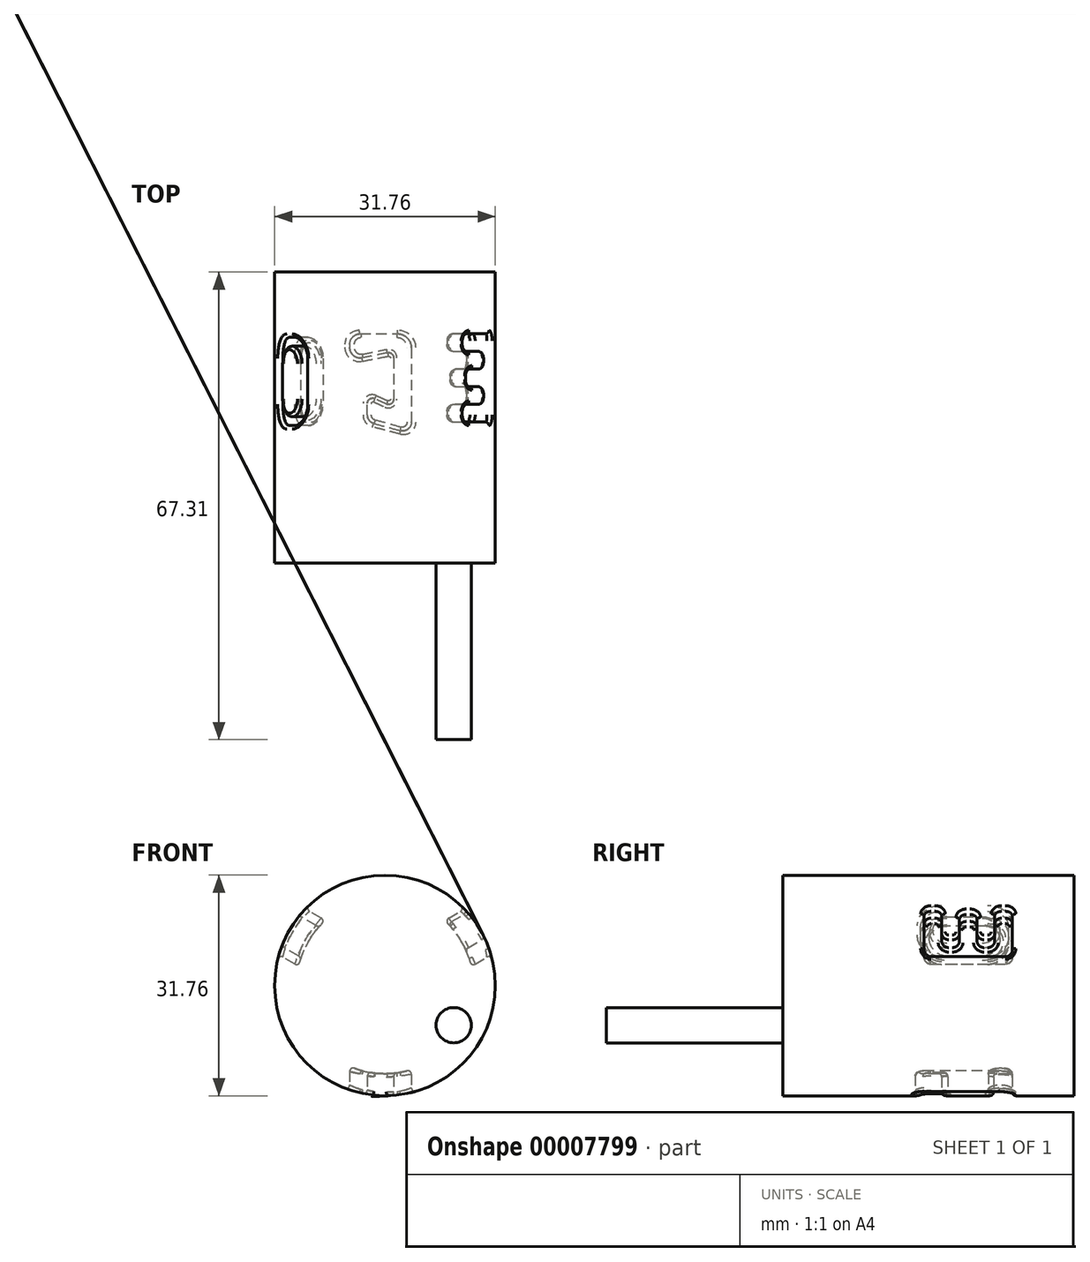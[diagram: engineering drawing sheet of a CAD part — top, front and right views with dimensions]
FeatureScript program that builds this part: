
annotation { "Feature Type Name" : "Feature", "Feature Type Description" : "" }
export const myFeature = defineFeature(function(context is Context, id is Id, definition is map)
    precondition{}
    {
        {
            var Q0;
            Q0=qCreatedBy(makeId("Front.planeOp"),FACE);
            var sketch = newSketch(context, id + "F0", { "sketchPlane" : qUnion([Q0])});
            skCircle(sketch, "E0", {"center": v(0, 0) * mm, "radius": 15.88 * mm});
            skSolve(sketch);
        }
        {
            var Q0;
            Q0=qSketchRegion(id+"F0",true);
            extrude(context, id + "F1", {"entities" : qUnion([Q0]), "depth" : 38.1 * mm});
        }
        {
            var Q0;
            Q0=qCreatedBy(makeId("Top.planeOp"),FACE);
            var sketch = newSketch(context, id + "F2", { "sketchPlane" : qUnion([Q0])});
            skLineSegment(sketch, "E1", {"start": v(-7.62, -35.56) * mm, "end": v(0, -24.13) * mm});
            skLineSegment(sketch, "E2", {"start": v(0, -24.13) * mm, "end": v(7.62, -35.56) * mm});
            skLineSegment(sketch, "E3", {"start": v(-8.9, -5.08) * mm, "end": v(-8.9, 0) * mm});
            skLineSegment(sketch, "E4", {"start": v(-8.9, 0) * mm, "end": v(0, -5.08) * mm});
            skLineSegment(sketch, "E5", {"start": v(0, -5.08) * mm, "end": v(8.89, 0) * mm});
            skLineSegment(sketch, "E6", {"start": v(8.9, 0) * mm, "end": v(8.9, -5.08) * mm});
            skArc(sketch, "E7", {"start": v(-8.9, -15.24) * mm, "mid": v(-10.64, -25.55) * mm, "end": v(-7.62, -35.56) * mm});
            skArc(sketch, "E8", {"start": v(7.62, -35.56) * mm, "mid": v(10.64, -25.55) * mm, "end": v(8.9, -15.24) * mm});
            skArc(sketch, "E9", {"start": v(8.9, -15.24) * mm, "mid": v(12.14, -9.84) * mm, "end": v(13.97, -3.8) * mm});
            skArc(sketch, "E10", {"start": v(-13.97, -3.81) * mm, "mid": v(-12.14, -9.84) * mm, "end": v(-8.9, -15.24) * mm});
            skLineSegment(sketch, "E11", {"start": v(8.9, -5.08) * mm, "end": v(13.97, -3.8) * mm});
            skLineSegment(sketch, "E12", {"start": v(-13.97, -3.81) * mm, "end": v(-8.9, -5.08) * mm});
            skLineSegment(sketch, "E13", {"start": v(0, -24.13) * mm, "end": v(0, -5.08) * mm});
            skSolve(sketch);
        }
        {
            var Q0;
            Q0=qCreatedBy(makeId("Top.planeOp"),FACE);
            cPlane(context, id + "F3", {"entities" : qUnion([Q0]), "cplaneType" : CPlaneType.OFFSET, "offset" : 15.88 * mm, "oppositeDirection" : true, "width" : 152.4 * mm, "height" : 152.4 * mm});
        }
        {
            var Q0;
            Q0=qCreatedBy(id+"F3.planeOp",FACE);
            var sketch = newSketch(context, id + "F4", { "sketchPlane" : qUnion([Q0])});
            skLineSegment(sketch, "E14", {"start": v(3.81, -21.59) * mm, "end": v(3.8, -10.92) * mm});
            skLineSegment(sketch, "E15", {"start": v(1.78, -8.9) * mm, "end": v(-3.56, -8.9) * mm});
            skPoint(sketch, "E16.visualSharp", {"position": v(3.81, -21.59) * mm});
            skPoint(sketch, "E17.visualSharp", {"position": v(3.8, -8.9) * mm});
            skArc(sketch, "E17.filletArc", {"start": v(3.81, -10.92) * mm, "mid": v(3.21, -9.49) * mm, "end": v(1.78, -8.9) * mm});
            skLineSegment(sketch, "E18", {"start": v(-5.08, -10.41) * mm, "end": v(-5.08, -10.84) * mm});
            skLineSegment(sketch, "E19", {"start": v(-3.26, -12.34) * mm, "end": v(0.36, -11.61) * mm});
            skLineSegment(sketch, "E20", {"start": v(1.27, -12.36) * mm, "end": v(1.27, -18.29) * mm});
            skPoint(sketch, "E21.visualSharp", {"position": v(-5.08, -12.7) * mm});
            skArc(sketch, "E21.filletArc", {"start": v(-5.08, -10.84) * mm, "mid": v(-4.52, -12.02) * mm, "end": v(-3.26, -12.34) * mm});
            skPoint(sketch, "E22.visualSharp", {"position": v(-5.08, -8.9) * mm});
            skArc(sketch, "E22.filletArc", {"start": v(-3.56, -8.89) * mm, "mid": v(-4.63, -9.34) * mm, "end": v(-5.08, -10.41) * mm});
            skPoint(sketch, "E23.visualSharp", {"position": v(1.27, -11.43) * mm});
            skArc(sketch, "E23.filletArc", {"start": v(1.27, -12.36) * mm, "mid": v(1, -11.77) * mm, "end": v(0.36, -11.61) * mm});
            skLineSegment(sketch, "E24", {"start": v(2.21, -22.82) * mm, "end": v(-1.6, -21.8) * mm});
            skLineSegment(sketch, "E25", {"start": v(-2.54, -20.57) * mm, "end": v(-2.54, -18.92) * mm});
            skLineSegment(sketch, "E26", {"start": v(-1.46, -18.23) * mm, "end": v(0.2, -18.98) * mm});
            skArc(sketch, "E27.filletArc", {"start": v(2.21, -22.82) * mm, "mid": v(3.31, -22.6) * mm, "end": v(3.81, -21.59) * mm});
            skPoint(sketch, "E28.visualSharp", {"position": v(-2.54, -21.54) * mm});
            skArc(sketch, "E28.filletArc", {"start": v(-2.54, -20.57) * mm, "mid": v(-2.28, -21.34) * mm, "end": v(-1.6, -21.8) * mm});
            skPoint(sketch, "E29.visualSharp", {"position": v(-2.54, -17.73) * mm});
            skArc(sketch, "E29.filletArc", {"start": v(-1.46, -18.23) * mm, "mid": v(-2.2, -18.28) * mm, "end": v(-2.54, -18.92) * mm});
            skPoint(sketch, "E30.visualSharp", {"position": v(1.27, -19.47) * mm});
            skArc(sketch, "E30.filletArc", {"start": v(0.2, -18.98) * mm, "mid": v(0.92, -18.93) * mm, "end": v(1.27, -18.29) * mm});
            skSolve(sketch);
        }
        {
            var Q0;
            Q0=qSketchRegion(id+"F4",true);
            extrude(context, id + "F5", {"entities" : qUnion([Q0]), "depth" : 25.4 * mm});
        }
        {
            var Q0;
            Q0=makeQuery(id+"F1.opExtrude","CAP_FACE",FACE,{"disambiguationData":[OSD([sQuery(id+"F0.wireOp",EDGE,"E0")])],"isStart":false});
            var sketch = newSketch(context, id + "F6", { "sketchPlane" : qUnion([Q0])});
            skCircle(sketch, "E31", {"center": v(0, 0) * mm, "radius": 12.7 * mm});
            skSolve(sketch);
        }
        {
            var Q0;
            Q0=qSketchRegion(id+"F6",true);
            extrude(context, id + "F7", {"entities" : qUnion([Q0]), "oppositeDirection" : true, "depth" : 38.1 * mm});
        }
        {
            var Q0;
            Q0=makeQuery(id+"F7.opExtrude","SWEPT_BODY",BODY,{"disambiguationData":[OSD([sQuery(id+"F6.wireOp",EDGE,"E31")])]});
            var Q1;
            Q1=makeQuery(id+"F5.opExtrude","SWEPT_BODY",BODY,{"disambiguationData":[OSD([sQuery(id+"F4.wireOp",EDGE,"E14"),sQuery(id+"F4.wireOp",EDGE,"E15"),sQuery(id+"F4.wireOp",EDGE,"E17.filletArc"),sQuery(id+"F4.wireOp",EDGE,"E18"),sQuery(id+"F4.wireOp",EDGE,"E19"),sQuery(id+"F4.wireOp",EDGE,"E20"),sQuery(id+"F4.wireOp",EDGE,"E21.filletArc"),sQuery(id+"F4.wireOp",EDGE,"E22.filletArc"),sQuery(id+"F4.wireOp",EDGE,"E23.filletArc"),sQuery(id+"F4.wireOp",EDGE,"E24"),sQuery(id+"F4.wireOp",EDGE,"E25"),sQuery(id+"F4.wireOp",EDGE,"E26"),sQuery(id+"F4.wireOp",EDGE,"E27.filletArc"),sQuery(id+"F4.wireOp",EDGE,"E28.filletArc"),sQuery(id+"F4.wireOp",EDGE,"E29.filletArc"),sQuery(id+"F4.wireOp",EDGE,"E30.filletArc")])]});
            booleanBodies(context, id + "F8", {"operationType" : BooleanOperationType.SUBTRACTION, "tools" : qUnion([Q0]), "targets" : qUnion([Q1]), "keepTools" : true});
        }
        {
            var Q0;
            Q0=makeQuery(id+"F5.opExtrude","SWEPT_BODY",BODY,{"disambiguationData":[OSD([sQuery(id+"F4.wireOp",EDGE,"E14"),sQuery(id+"F4.wireOp",EDGE,"E15"),sQuery(id+"F4.wireOp",EDGE,"E17.filletArc"),sQuery(id+"F4.wireOp",EDGE,"E18"),sQuery(id+"F4.wireOp",EDGE,"E19"),sQuery(id+"F4.wireOp",EDGE,"E20"),sQuery(id+"F4.wireOp",EDGE,"E21.filletArc"),sQuery(id+"F4.wireOp",EDGE,"E22.filletArc"),sQuery(id+"F4.wireOp",EDGE,"E23.filletArc"),sQuery(id+"F4.wireOp",EDGE,"E24"),sQuery(id+"F4.wireOp",EDGE,"E25"),sQuery(id+"F4.wireOp",EDGE,"E26"),sQuery(id+"F4.wireOp",EDGE,"E27.filletArc"),sQuery(id+"F4.wireOp",EDGE,"E28.filletArc"),sQuery(id+"F4.wireOp",EDGE,"E29.filletArc"),sQuery(id+"F4.wireOp",EDGE,"E30.filletArc")])]});
            var Q1;
            Q1=makeQuery(id+"F1.opExtrude","SWEPT_BODY",BODY,{"disambiguationData":[OSD([sQuery(id+"F0.wireOp",EDGE,"E0")])]});
            booleanBodies(context, id + "F9", {"operationType" : BooleanOperationType.SUBTRACTION, "tools" : qUnion([Q0]), "targets" : qUnion([Q1])});
        }
        {
            var Q0;
            Q0=makeQuery(id+"F9.opBoolean","COPY",EDGE,{"derivedFrom":makeQuery(id+"F8.opBoolean","INTERSECT",EDGE,{"derivedFrom":[makeQuery(id+"F5.opExtrude","SWEPT_FACE",FACE,{"disambiguationData":[OSD([sQuery(id+"F4.wireOp",EDGE,"E20")])]}),makeQuery(id+"F7.opExtrude","SWEPT_FACE",FACE,{"disambiguationData":[OSD([sQuery(id+"F6.wireOp",EDGE,"E31")])]})]})});
            var Q1;
            Q1=makeQuery(id+"F9.opBoolean","COPY",EDGE,{"derivedFrom":makeQuery(id+"F8.opBoolean","INTERSECT",EDGE,{"derivedFrom":[makeQuery(id+"F5.opExtrude","SWEPT_FACE",FACE,{"disambiguationData":[OSD([sQuery(id+"F4.wireOp",EDGE,"E30.filletArc")])]}),makeQuery(id+"F7.opExtrude","SWEPT_FACE",FACE,{"disambiguationData":[OSD([sQuery(id+"F6.wireOp",EDGE,"E31")])]})]})});
            var Q2;
            Q2=makeQuery(id+"F9.opBoolean","COPY",EDGE,{"derivedFrom":makeQuery(id+"F8.opBoolean","INTERSECT",EDGE,{"derivedFrom":[makeQuery(id+"F5.opExtrude","SWEPT_FACE",FACE,{"disambiguationData":[OSD([sQuery(id+"F4.wireOp",EDGE,"E26")])]}),makeQuery(id+"F7.opExtrude","SWEPT_FACE",FACE,{"disambiguationData":[OSD([sQuery(id+"F6.wireOp",EDGE,"E31")])]})]})});
            var Q3;
            Q3=makeQuery(id+"F9.opBoolean","COPY",EDGE,{"derivedFrom":makeQuery(id+"F8.opBoolean","INTERSECT",EDGE,{"derivedFrom":[makeQuery(id+"F5.opExtrude","SWEPT_FACE",FACE,{"disambiguationData":[OSD([sQuery(id+"F4.wireOp",EDGE,"E29.filletArc")])]}),makeQuery(id+"F7.opExtrude","SWEPT_FACE",FACE,{"disambiguationData":[OSD([sQuery(id+"F6.wireOp",EDGE,"E31")])]})]})});
            var Q4;
            Q4=makeQuery(id+"F9.opBoolean","COPY",EDGE,{"derivedFrom":makeQuery(id+"F8.opBoolean","INTERSECT",EDGE,{"derivedFrom":[makeQuery(id+"F5.opExtrude","SWEPT_FACE",FACE,{"disambiguationData":[OSD([sQuery(id+"F4.wireOp",EDGE,"E25")])]}),makeQuery(id+"F7.opExtrude","SWEPT_FACE",FACE,{"disambiguationData":[OSD([sQuery(id+"F6.wireOp",EDGE,"E31")])]})]})});
            var Q5;
            Q5=makeQuery(id+"F9.opBoolean","COPY",EDGE,{"derivedFrom":makeQuery(id+"F8.opBoolean","INTERSECT",EDGE,{"derivedFrom":[makeQuery(id+"F5.opExtrude","SWEPT_FACE",FACE,{"disambiguationData":[OSD([sQuery(id+"F4.wireOp",EDGE,"E28.filletArc")])]}),makeQuery(id+"F7.opExtrude","SWEPT_FACE",FACE,{"disambiguationData":[OSD([sQuery(id+"F6.wireOp",EDGE,"E31")])]})]})});
            var Q6;
            Q6=makeQuery(id+"F9.opBoolean","COPY",EDGE,{"derivedFrom":makeQuery(id+"F8.opBoolean","INTERSECT",EDGE,{"derivedFrom":[makeQuery(id+"F5.opExtrude","SWEPT_FACE",FACE,{"disambiguationData":[OSD([sQuery(id+"F4.wireOp",EDGE,"E24")])]}),makeQuery(id+"F7.opExtrude","SWEPT_FACE",FACE,{"disambiguationData":[OSD([sQuery(id+"F6.wireOp",EDGE,"E31")])]})]})});
            var Q7;
            Q7=makeQuery(id+"F9.opBoolean","COPY",EDGE,{"derivedFrom":makeQuery(id+"F8.opBoolean","INTERSECT",EDGE,{"derivedFrom":[makeQuery(id+"F5.opExtrude","SWEPT_FACE",FACE,{"disambiguationData":[OSD([sQuery(id+"F4.wireOp",EDGE,"E27.filletArc")])]}),makeQuery(id+"F7.opExtrude","SWEPT_FACE",FACE,{"disambiguationData":[OSD([sQuery(id+"F6.wireOp",EDGE,"E31")])]})]})});
            var Q8;
            Q8=makeQuery(id+"F9.opBoolean","COPY",EDGE,{"derivedFrom":makeQuery(id+"F8.opBoolean","INTERSECT",EDGE,{"derivedFrom":[makeQuery(id+"F5.opExtrude","SWEPT_FACE",FACE,{"disambiguationData":[OSD([sQuery(id+"F4.wireOp",EDGE,"E14")])]}),makeQuery(id+"F7.opExtrude","SWEPT_FACE",FACE,{"disambiguationData":[OSD([sQuery(id+"F6.wireOp",EDGE,"E31")])]})]})});
            var Q9;
            Q9=makeQuery(id+"F9.opBoolean","COPY",EDGE,{"derivedFrom":makeQuery(id+"F8.opBoolean","INTERSECT",EDGE,{"derivedFrom":[makeQuery(id+"F5.opExtrude","SWEPT_FACE",FACE,{"disambiguationData":[OSD([sQuery(id+"F4.wireOp",EDGE,"E17.filletArc")])]}),makeQuery(id+"F7.opExtrude","SWEPT_FACE",FACE,{"disambiguationData":[OSD([sQuery(id+"F6.wireOp",EDGE,"E31")])]})]})});
            var Q10;
            Q10=makeQuery(id+"F9.opBoolean","COPY",EDGE,{"derivedFrom":makeQuery(id+"F8.opBoolean","INTERSECT",EDGE,{"derivedFrom":[makeQuery(id+"F5.opExtrude","SWEPT_FACE",FACE,{"disambiguationData":[OSD([sQuery(id+"F4.wireOp",EDGE,"E15")])]}),makeQuery(id+"F7.opExtrude","SWEPT_FACE",FACE,{"disambiguationData":[OSD([sQuery(id+"F6.wireOp",EDGE,"E31")])]})]})});
            var Q11;
            Q11=makeQuery(id+"F9.opBoolean","COPY",EDGE,{"derivedFrom":makeQuery(id+"F8.opBoolean","INTERSECT",EDGE,{"derivedFrom":[makeQuery(id+"F5.opExtrude","SWEPT_FACE",FACE,{"disambiguationData":[OSD([sQuery(id+"F4.wireOp",EDGE,"E22.filletArc")])]}),makeQuery(id+"F7.opExtrude","SWEPT_FACE",FACE,{"disambiguationData":[OSD([sQuery(id+"F6.wireOp",EDGE,"E31")])]})]})});
            var Q12;
            Q12=makeQuery(id+"F9.opBoolean","COPY",EDGE,{"derivedFrom":makeQuery(id+"F8.opBoolean","INTERSECT",EDGE,{"derivedFrom":[makeQuery(id+"F5.opExtrude","SWEPT_FACE",FACE,{"disambiguationData":[OSD([sQuery(id+"F4.wireOp",EDGE,"E18")])]}),makeQuery(id+"F7.opExtrude","SWEPT_FACE",FACE,{"disambiguationData":[OSD([sQuery(id+"F6.wireOp",EDGE,"E31")])]})]})});
            var Q13;
            Q13=makeQuery(id+"F9.opBoolean","COPY",EDGE,{"derivedFrom":makeQuery(id+"F8.opBoolean","INTERSECT",EDGE,{"derivedFrom":[makeQuery(id+"F5.opExtrude","SWEPT_FACE",FACE,{"disambiguationData":[OSD([sQuery(id+"F4.wireOp",EDGE,"E21.filletArc")])]}),makeQuery(id+"F7.opExtrude","SWEPT_FACE",FACE,{"disambiguationData":[OSD([sQuery(id+"F6.wireOp",EDGE,"E31")])]})]})});
            var Q14;
            Q14=makeQuery(id+"F9.opBoolean","COPY",EDGE,{"derivedFrom":makeQuery(id+"F8.opBoolean","INTERSECT",EDGE,{"derivedFrom":[makeQuery(id+"F5.opExtrude","SWEPT_FACE",FACE,{"disambiguationData":[OSD([sQuery(id+"F4.wireOp",EDGE,"E19")])]}),makeQuery(id+"F7.opExtrude","SWEPT_FACE",FACE,{"disambiguationData":[OSD([sQuery(id+"F6.wireOp",EDGE,"E31")])]})]})});
            var Q15;
            Q15=makeQuery(id+"F9.opBoolean","COPY",EDGE,{"derivedFrom":makeQuery(id+"F8.opBoolean","INTERSECT",EDGE,{"derivedFrom":[makeQuery(id+"F5.opExtrude","SWEPT_FACE",FACE,{"disambiguationData":[OSD([sQuery(id+"F4.wireOp",EDGE,"E23.filletArc")])]}),makeQuery(id+"F7.opExtrude","SWEPT_FACE",FACE,{"disambiguationData":[OSD([sQuery(id+"F6.wireOp",EDGE,"E31")])]})]})});
            fillet(context, id + "F10", {"entities" : qUnion([Q0, Q1, Q2, Q3, Q4, Q5, Q6, Q7, Q8, Q9, Q10, Q11, Q12, Q13, Q14, Q15]), "radius" : 0.5 * mm, "tangentPropagation" : true, "allowEdgeOverflow" : false});
        }
        {
            var Q0;
            Q0=makeQuery(id+"F9.opBoolean","INTERSECT",EDGE,{"derivedFrom":[makeQuery(id+"F1.opExtrude","SWEPT_FACE",FACE,{"disambiguationData":[OSD([sQuery(id+"F0.wireOp",EDGE,"E0")])]}),makeQuery(id+"F5.opExtrude","SWEPT_FACE",FACE,{"disambiguationData":[OSD([sQuery(id+"F4.wireOp",EDGE,"E14")])]})]});
            var Q1;
            Q1=makeQuery(id+"F9.opBoolean","INTERSECT",EDGE,{"derivedFrom":[makeQuery(id+"F1.opExtrude","SWEPT_FACE",FACE,{"disambiguationData":[OSD([sQuery(id+"F0.wireOp",EDGE,"E0")])]}),makeQuery(id+"F5.opExtrude","SWEPT_FACE",FACE,{"disambiguationData":[OSD([sQuery(id+"F4.wireOp",EDGE,"E27.filletArc")])]})]});
            var Q2;
            Q2=makeQuery(id+"F9.opBoolean","INTERSECT",EDGE,{"derivedFrom":[makeQuery(id+"F1.opExtrude","SWEPT_FACE",FACE,{"disambiguationData":[OSD([sQuery(id+"F0.wireOp",EDGE,"E0")])]}),makeQuery(id+"F5.opExtrude","SWEPT_FACE",FACE,{"disambiguationData":[OSD([sQuery(id+"F4.wireOp",EDGE,"E24")])]})]});
            var Q3;
            Q3=makeQuery(id+"F9.opBoolean","INTERSECT",EDGE,{"derivedFrom":[makeQuery(id+"F1.opExtrude","SWEPT_FACE",FACE,{"disambiguationData":[OSD([sQuery(id+"F0.wireOp",EDGE,"E0")])]}),makeQuery(id+"F5.opExtrude","SWEPT_FACE",FACE,{"disambiguationData":[OSD([sQuery(id+"F4.wireOp",EDGE,"E28.filletArc")])]})]});
            var Q4;
            Q4=makeQuery(id+"F9.opBoolean","INTERSECT",EDGE,{"derivedFrom":[makeQuery(id+"F1.opExtrude","SWEPT_FACE",FACE,{"disambiguationData":[OSD([sQuery(id+"F0.wireOp",EDGE,"E0")])]}),makeQuery(id+"F5.opExtrude","SWEPT_FACE",FACE,{"disambiguationData":[OSD([sQuery(id+"F4.wireOp",EDGE,"E25")])]})]});
            var Q5;
            Q5=makeQuery(id+"F9.opBoolean","INTERSECT",EDGE,{"derivedFrom":[makeQuery(id+"F1.opExtrude","SWEPT_FACE",FACE,{"disambiguationData":[OSD([sQuery(id+"F0.wireOp",EDGE,"E0")])]}),makeQuery(id+"F5.opExtrude","SWEPT_FACE",FACE,{"disambiguationData":[OSD([sQuery(id+"F4.wireOp",EDGE,"E29.filletArc")])]})]});
            var Q6;
            Q6=makeQuery(id+"F9.opBoolean","INTERSECT",EDGE,{"derivedFrom":[makeQuery(id+"F1.opExtrude","SWEPT_FACE",FACE,{"disambiguationData":[OSD([sQuery(id+"F0.wireOp",EDGE,"E0")])]}),makeQuery(id+"F5.opExtrude","SWEPT_FACE",FACE,{"disambiguationData":[OSD([sQuery(id+"F4.wireOp",EDGE,"E26")])]})]});
            var Q7;
            Q7=makeQuery(id+"F9.opBoolean","INTERSECT",EDGE,{"derivedFrom":[makeQuery(id+"F1.opExtrude","SWEPT_FACE",FACE,{"disambiguationData":[OSD([sQuery(id+"F0.wireOp",EDGE,"E0")])]}),makeQuery(id+"F5.opExtrude","SWEPT_FACE",FACE,{"disambiguationData":[OSD([sQuery(id+"F4.wireOp",EDGE,"E30.filletArc")])]})]});
            var Q8;
            Q8=makeQuery(id+"F9.opBoolean","INTERSECT",EDGE,{"derivedFrom":[makeQuery(id+"F1.opExtrude","SWEPT_FACE",FACE,{"disambiguationData":[OSD([sQuery(id+"F0.wireOp",EDGE,"E0")])]}),makeQuery(id+"F5.opExtrude","SWEPT_FACE",FACE,{"disambiguationData":[OSD([sQuery(id+"F4.wireOp",EDGE,"E20")])]})]});
            var Q9;
            Q9=makeQuery(id+"F9.opBoolean","INTERSECT",EDGE,{"derivedFrom":[makeQuery(id+"F1.opExtrude","SWEPT_FACE",FACE,{"disambiguationData":[OSD([sQuery(id+"F0.wireOp",EDGE,"E0")])]}),makeQuery(id+"F5.opExtrude","SWEPT_FACE",FACE,{"disambiguationData":[OSD([sQuery(id+"F4.wireOp",EDGE,"E19")])]})]});
            var Q10;
            Q10=makeQuery(id+"F9.opBoolean","INTERSECT",EDGE,{"derivedFrom":[makeQuery(id+"F1.opExtrude","SWEPT_FACE",FACE,{"disambiguationData":[OSD([sQuery(id+"F0.wireOp",EDGE,"E0")])]}),makeQuery(id+"F5.opExtrude","SWEPT_FACE",FACE,{"disambiguationData":[OSD([sQuery(id+"F4.wireOp",EDGE,"E23.filletArc")])]})]});
            var Q11;
            Q11=makeQuery(id+"F9.opBoolean","INTERSECT",EDGE,{"derivedFrom":[makeQuery(id+"F1.opExtrude","SWEPT_FACE",FACE,{"disambiguationData":[OSD([sQuery(id+"F0.wireOp",EDGE,"E0")])]}),makeQuery(id+"F5.opExtrude","SWEPT_FACE",FACE,{"disambiguationData":[OSD([sQuery(id+"F4.wireOp",EDGE,"E21.filletArc")])]})]});
            var Q12;
            Q12=makeQuery(id+"F9.opBoolean","INTERSECT",EDGE,{"derivedFrom":[makeQuery(id+"F1.opExtrude","SWEPT_FACE",FACE,{"disambiguationData":[OSD([sQuery(id+"F0.wireOp",EDGE,"E0")])]}),makeQuery(id+"F5.opExtrude","SWEPT_FACE",FACE,{"disambiguationData":[OSD([sQuery(id+"F4.wireOp",EDGE,"E18")])]})]});
            var Q13;
            Q13=makeQuery(id+"F9.opBoolean","INTERSECT",EDGE,{"derivedFrom":[makeQuery(id+"F1.opExtrude","SWEPT_FACE",FACE,{"disambiguationData":[OSD([sQuery(id+"F0.wireOp",EDGE,"E0")])]}),makeQuery(id+"F5.opExtrude","SWEPT_FACE",FACE,{"disambiguationData":[OSD([sQuery(id+"F4.wireOp",EDGE,"E22.filletArc")])]})]});
            var Q14;
            Q14=makeQuery(id+"F9.opBoolean","INTERSECT",EDGE,{"derivedFrom":[makeQuery(id+"F1.opExtrude","SWEPT_FACE",FACE,{"disambiguationData":[OSD([sQuery(id+"F0.wireOp",EDGE,"E0")])]}),makeQuery(id+"F5.opExtrude","SWEPT_FACE",FACE,{"disambiguationData":[OSD([sQuery(id+"F4.wireOp",EDGE,"E15")])]})]});
            var Q15;
            Q15=makeQuery(id+"F9.opBoolean","INTERSECT",EDGE,{"derivedFrom":[makeQuery(id+"F1.opExtrude","SWEPT_FACE",FACE,{"disambiguationData":[OSD([sQuery(id+"F0.wireOp",EDGE,"E0")])]}),makeQuery(id+"F5.opExtrude","SWEPT_FACE",FACE,{"disambiguationData":[OSD([sQuery(id+"F4.wireOp",EDGE,"E17.filletArc")])]})]});
            fillet(context, id + "F11", {"entities" : qUnion([Q0, Q1, Q2, Q3, Q4, Q5, Q6, Q7, Q8, Q9, Q10, Q11, Q12, Q13, Q14, Q15]), "radius" : 0.5 * mm, "tangentPropagation" : true, "allowEdgeOverflow" : false});
        }
        {
            var Q0;
            Q0=makeQuery(id+"F2.imprint","IMPRINT",FACE,{"disambiguationData":[TD([[makeQuery(id+"F2.imprint","IMPRINT",EDGE,{"derivedFrom":sQuery(id+"F2.wireOp",EDGE,"E2")}),1.0]])]});
            var Q1;
            Q1=sQuery(id+"F2.wireOp",EDGE,"E1");
            var Q2;
            Q2=sQuery(id+"F2.wireOp",EDGE,"E7");
            var Q3;
            Q3=sQuery(id+"F2.wireOp",EDGE,"E10");
            var Q4;
            Q4=sQuery(id+"F2.wireOp",EDGE,"E12");
            var Q5;
            Q5=sQuery(id+"F2.wireOp",EDGE,"E3");
            var Q6;
            Q6=sQuery(id+"F2.wireOp",EDGE,"E4");
            var Q7;
            Q7=sQuery(id+"F2.wireOp",EDGE,"E13");
            revolve(context, id + "F12", {"bodyType" : ToolBodyType.SURFACE, "entities" : qUnion([Q0]), "surfaceEntities" : qUnion([Q1, Q2, Q3, Q4, Q5, Q6]), "axis" : qUnion([Q7]), "revolveType" : RevolveType.ONE_DIRECTION, "angle" : 120 * degree});
        }
        {
            var Q0;
            Q0=sQuery(id+"F2.wireOp",EDGE,"E13");
            cPlane(context, id + "F13", {"entities" : qUnion([Q0]), "cplaneType" : CPlaneType.LINE_ANGLE, "offset" : 152.4 * mm, "angle" : 120 * degree, "width" : 152.4 * mm, "height" : 152.4 * mm});
        }
        {
            var Q0;
            Q0=qCreatedBy(id+"F13.planeOp",FACE);
            cPlane(context, id + "F14", {"entities" : qUnion([Q0]), "cplaneType" : CPlaneType.OFFSET, "offset" : 15.88 * mm, "oppositeDirection" : true, "width" : 152.4 * mm, "height" : 152.4 * mm});
        }
        {
            var Q0;
            Q0=qCreatedBy(id+"F14.planeOp",FACE);
            var sketch = newSketch(context, id + "F15", { "sketchPlane" : qUnion([Q0])});
            skLineSegment(sketch, "E32", {"start": v(-19.05, 3.8) * mm, "end": v(-12.45, 3.8) * mm});
            skLineSegment(sketch, "E33", {"start": v(-9.4, 0.76) * mm, "end": v(-9.4, -0.76) * mm});
            skLineSegment(sketch, "E34", {"start": v(-12.45, -3.81) * mm, "end": v(-19.05, -3.81) * mm});
            skLineSegment(sketch, "E35", {"start": v(-22.1, -0.76) * mm, "end": v(-22.1, 0.76) * mm});
            skPoint(sketch, "E36.visualSharp", {"position": v(-22.1, 3.8) * mm});
            skArc(sketch, "E36.filletArc", {"start": v(-19.05, 3.8) * mm, "mid": v(-21.2, 2.92) * mm, "end": v(-22.1, 0.76) * mm});
            skPoint(sketch, "E37.visualSharp", {"position": v(-22.1, -3.81) * mm});
            skArc(sketch, "E37.filletArc", {"start": v(-22.1, -0.76) * mm, "mid": v(-21.2, -2.92) * mm, "end": v(-19.05, -3.81) * mm});
            skPoint(sketch, "E38.visualSharp", {"position": v(-9.4, 3.8) * mm});
            skArc(sketch, "E38.filletArc", {"start": v(-9.4, 0.76) * mm, "mid": v(-10.3, 2.92) * mm, "end": v(-12.45, 3.8) * mm});
            skPoint(sketch, "E39.visualSharp", {"position": v(-9.4, -3.81) * mm});
            skArc(sketch, "E39.filletArc", {"start": v(-12.45, -3.81) * mm, "mid": v(-10.3, -2.92) * mm, "end": v(-9.4, -0.76) * mm});
            skLineSegment(sketch, "E40", {"start": v(-18.29, 2.54) * mm, "end": v(-13.2, 2.54) * mm});
            skLineSegment(sketch, "E41", {"start": v(-10.67, 0) * mm, "end": v(-10.67, 0) * mm});
            skLineSegment(sketch, "E42", {"start": v(-13.2, -2.54) * mm, "end": v(-18.29, -2.54) * mm});
            skLineSegment(sketch, "E43", {"start": v(-20.83, 0) * mm, "end": v(-20.83, 0) * mm});
            skPoint(sketch, "E44.visualSharp", {"position": v(-20.83, 2.54) * mm});
            skArc(sketch, "E44.filletArc", {"start": v(-18.29, 2.54) * mm, "mid": v(-20.08, 1.8) * mm, "end": v(-20.83, 0) * mm});
            skPoint(sketch, "E45.visualSharp", {"position": v(-20.83, -2.54) * mm});
            skArc(sketch, "E45.filletArc", {"start": v(-20.83, 0) * mm, "mid": v(-20.08, -1.8) * mm, "end": v(-18.29, -2.54) * mm});
            skPoint(sketch, "E46.visualSharp", {"position": v(-10.67, 2.54) * mm});
            skArc(sketch, "E46.filletArc", {"start": v(-10.67, 0) * mm, "mid": v(-11.41, 1.8) * mm, "end": v(-13.2, 2.54) * mm});
            skPoint(sketch, "E47.visualSharp", {"position": v(-10.67, -2.54) * mm});
            skArc(sketch, "E47.filletArc", {"start": v(-13.2, -2.54) * mm, "mid": v(-11.41, -1.8) * mm, "end": v(-10.67, 0) * mm});
            skSolve(sketch);
        }
        {
            var Q0;
            Q0=qSketchRegion(id+"F15",true);
            extrude(context, id + "F16", {"entities" : qUnion([Q0]), "depth" : 25.4 * mm});
        }
        {
            var Q0;
            Q0=makeQuery(id+"F7.opExtrude","SWEPT_BODY",BODY,{"disambiguationData":[OSD([sQuery(id+"F6.wireOp",EDGE,"E31")])]});
            var Q1;
            Q1=makeQuery(id+"F16.opExtrude","SWEPT_BODY",BODY,{"disambiguationData":[OSD([sQuery(id+"F15.wireOp",EDGE,"E32"),sQuery(id+"F15.wireOp",EDGE,"E33"),sQuery(id+"F15.wireOp",EDGE,"E34"),sQuery(id+"F15.wireOp",EDGE,"E35"),sQuery(id+"F15.wireOp",EDGE,"E36.filletArc"),sQuery(id+"F15.wireOp",EDGE,"E37.filletArc"),sQuery(id+"F15.wireOp",EDGE,"E38.filletArc"),sQuery(id+"F15.wireOp",EDGE,"E39.filletArc"),sQuery(id+"F15.wireOp",EDGE,"E40"),sQuery(id+"F15.wireOp",EDGE,"E42"),sQuery(id+"F15.wireOp",EDGE,"E44.filletArc"),sQuery(id+"F15.wireOp",EDGE,"E45.filletArc"),sQuery(id+"F15.wireOp",EDGE,"E46.filletArc"),sQuery(id+"F15.wireOp",EDGE,"E47.filletArc")])]});
            booleanBodies(context, id + "F17", {"operationType" : BooleanOperationType.SUBTRACTION, "tools" : qUnion([Q0]), "targets" : qUnion([Q1]), "keepTools" : true});
        }
        {
            var Q0;
            Q0=makeQuery(id+"F16.opExtrude","SWEPT_BODY",BODY,{"disambiguationData":[OSD([sQuery(id+"F15.wireOp",EDGE,"E32"),sQuery(id+"F15.wireOp",EDGE,"E33"),sQuery(id+"F15.wireOp",EDGE,"E34"),sQuery(id+"F15.wireOp",EDGE,"E35"),sQuery(id+"F15.wireOp",EDGE,"E36.filletArc"),sQuery(id+"F15.wireOp",EDGE,"E37.filletArc"),sQuery(id+"F15.wireOp",EDGE,"E38.filletArc"),sQuery(id+"F15.wireOp",EDGE,"E39.filletArc"),sQuery(id+"F15.wireOp",EDGE,"E40"),sQuery(id+"F15.wireOp",EDGE,"E42"),sQuery(id+"F15.wireOp",EDGE,"E44.filletArc"),sQuery(id+"F15.wireOp",EDGE,"E45.filletArc"),sQuery(id+"F15.wireOp",EDGE,"E46.filletArc"),sQuery(id+"F15.wireOp",EDGE,"E47.filletArc")])]});
            var Q1;
            Q1=makeQuery(id+"F1.opExtrude","SWEPT_BODY",BODY,{"disambiguationData":[OSD([sQuery(id+"F0.wireOp",EDGE,"E0")])]});
            booleanBodies(context, id + "F18", {"operationType" : BooleanOperationType.SUBTRACTION, "tools" : qUnion([Q0]), "targets" : qUnion([Q1])});
        }
        {
            var Q0;
            Q0=makeQuery(id+"F18.opBoolean","INTERSECT",EDGE,{"derivedFrom":[makeQuery(id+"F1.opExtrude","SWEPT_FACE",FACE,{"disambiguationData":[OSD([sQuery(id+"F0.wireOp",EDGE,"E0")])]}),makeQuery(id+"F16.opExtrude","SWEPT_FACE",FACE,{"disambiguationData":[OSD([sQuery(id+"F15.wireOp",EDGE,"E36.filletArc")])]})]});
            var Q1;
            Q1=makeQuery(id+"F18.opBoolean","INTERSECT",EDGE,{"derivedFrom":[makeQuery(id+"F1.opExtrude","SWEPT_FACE",FACE,{"disambiguationData":[OSD([sQuery(id+"F0.wireOp",EDGE,"E0")])]}),makeQuery(id+"F16.opExtrude","SWEPT_FACE",FACE,{"disambiguationData":[OSD([sQuery(id+"F15.wireOp",EDGE,"E35")])]})]});
            var Q2;
            Q2=makeQuery(id+"F18.opBoolean","INTERSECT",EDGE,{"derivedFrom":[makeQuery(id+"F1.opExtrude","SWEPT_FACE",FACE,{"disambiguationData":[OSD([sQuery(id+"F0.wireOp",EDGE,"E0")])]}),makeQuery(id+"F16.opExtrude","SWEPT_FACE",FACE,{"disambiguationData":[OSD([sQuery(id+"F15.wireOp",EDGE,"E37.filletArc")])]})]});
            var Q3;
            Q3=makeQuery(id+"F18.opBoolean","INTERSECT",EDGE,{"derivedFrom":[makeQuery(id+"F1.opExtrude","SWEPT_FACE",FACE,{"disambiguationData":[OSD([sQuery(id+"F0.wireOp",EDGE,"E0")])]}),makeQuery(id+"F16.opExtrude","SWEPT_FACE",FACE,{"disambiguationData":[OSD([sQuery(id+"F15.wireOp",EDGE,"E34")])]})]});
            var Q4;
            Q4=makeQuery(id+"F18.opBoolean","INTERSECT",EDGE,{"derivedFrom":[makeQuery(id+"F1.opExtrude","SWEPT_FACE",FACE,{"disambiguationData":[OSD([sQuery(id+"F0.wireOp",EDGE,"E0")])]}),makeQuery(id+"F16.opExtrude","SWEPT_FACE",FACE,{"disambiguationData":[OSD([sQuery(id+"F15.wireOp",EDGE,"E39.filletArc")])]})]});
            var Q5;
            Q5=makeQuery(id+"F18.opBoolean","INTERSECT",EDGE,{"derivedFrom":[makeQuery(id+"F1.opExtrude","SWEPT_FACE",FACE,{"disambiguationData":[OSD([sQuery(id+"F0.wireOp",EDGE,"E0")])]}),makeQuery(id+"F16.opExtrude","SWEPT_FACE",FACE,{"disambiguationData":[OSD([sQuery(id+"F15.wireOp",EDGE,"E33")])]})]});
            var Q6;
            Q6=makeQuery(id+"F18.opBoolean","INTERSECT",EDGE,{"derivedFrom":[makeQuery(id+"F1.opExtrude","SWEPT_FACE",FACE,{"disambiguationData":[OSD([sQuery(id+"F0.wireOp",EDGE,"E0")])]}),makeQuery(id+"F16.opExtrude","SWEPT_FACE",FACE,{"disambiguationData":[OSD([sQuery(id+"F15.wireOp",EDGE,"E38.filletArc")])]})]});
            var Q7;
            Q7=makeQuery(id+"F18.opBoolean","INTERSECT",EDGE,{"derivedFrom":[makeQuery(id+"F1.opExtrude","SWEPT_FACE",FACE,{"disambiguationData":[OSD([sQuery(id+"F0.wireOp",EDGE,"E0")])]}),makeQuery(id+"F16.opExtrude","SWEPT_FACE",FACE,{"disambiguationData":[OSD([sQuery(id+"F15.wireOp",EDGE,"E32")])]})]});
            var Q8;
            Q8=makeQuery(id+"F18.opBoolean","INTERSECT",EDGE,{"derivedFrom":[makeQuery(id+"F1.opExtrude","SWEPT_FACE",FACE,{"disambiguationData":[OSD([sQuery(id+"F0.wireOp",EDGE,"E0")])]}),makeQuery(id+"F16.opExtrude","SWEPT_FACE",FACE,{"disambiguationData":[OSD([sQuery(id+"F15.wireOp",EDGE,"E44.filletArc"),sQuery(id+"F15.wireOp",EDGE,"E45.filletArc")])]})]});
            var Q9;
            Q9=makeQuery(id+"F18.opBoolean","INTERSECT",EDGE,{"derivedFrom":[makeQuery(id+"F1.opExtrude","SWEPT_FACE",FACE,{"disambiguationData":[OSD([sQuery(id+"F0.wireOp",EDGE,"E0")])]}),makeQuery(id+"F16.opExtrude","SWEPT_FACE",FACE,{"disambiguationData":[OSD([sQuery(id+"F15.wireOp",EDGE,"E40")])]})]});
            var Q10;
            Q10=makeQuery(id+"F18.opBoolean","INTERSECT",EDGE,{"derivedFrom":[makeQuery(id+"F1.opExtrude","SWEPT_FACE",FACE,{"disambiguationData":[OSD([sQuery(id+"F0.wireOp",EDGE,"E0")])]}),makeQuery(id+"F16.opExtrude","SWEPT_FACE",FACE,{"disambiguationData":[OSD([sQuery(id+"F15.wireOp",EDGE,"E46.filletArc"),sQuery(id+"F15.wireOp",EDGE,"E47.filletArc")])]})]});
            var Q11;
            Q11=makeQuery(id+"F18.opBoolean","INTERSECT",EDGE,{"derivedFrom":[makeQuery(id+"F1.opExtrude","SWEPT_FACE",FACE,{"disambiguationData":[OSD([sQuery(id+"F0.wireOp",EDGE,"E0")])]}),makeQuery(id+"F16.opExtrude","SWEPT_FACE",FACE,{"disambiguationData":[OSD([sQuery(id+"F15.wireOp",EDGE,"E42")])]})]});
            fillet(context, id + "F19", {"entities" : qUnion([Q0, Q1, Q2, Q3, Q4, Q5, Q6, Q7, Q8, Q9, Q10, Q11]), "radius" : 0.5 * mm, "tangentPropagation" : true, "allowEdgeOverflow" : false});
        }
        {
            var Q0;
            Q0=makeQuery(id+"F18.opBoolean","COPY",EDGE,{"derivedFrom":makeQuery(id+"F17.opBoolean","INTERSECT",EDGE,{"derivedFrom":[makeQuery(id+"F7.opExtrude","SWEPT_FACE",FACE,{"disambiguationData":[OSD([sQuery(id+"F6.wireOp",EDGE,"E31")])]}),makeQuery(id+"F16.opExtrude","SWEPT_FACE",FACE,{"disambiguationData":[OSD([sQuery(id+"F15.wireOp",EDGE,"E36.filletArc")])]})]})});
            var Q1;
            Q1=makeQuery(id+"F18.opBoolean","COPY",EDGE,{"derivedFrom":makeQuery(id+"F17.opBoolean","INTERSECT",EDGE,{"derivedFrom":[makeQuery(id+"F7.opExtrude","SWEPT_FACE",FACE,{"disambiguationData":[OSD([sQuery(id+"F6.wireOp",EDGE,"E31")])]}),makeQuery(id+"F16.opExtrude","SWEPT_FACE",FACE,{"disambiguationData":[OSD([sQuery(id+"F15.wireOp",EDGE,"E35")])]})]})});
            var Q2;
            Q2=makeQuery(id+"F18.opBoolean","COPY",EDGE,{"derivedFrom":makeQuery(id+"F17.opBoolean","INTERSECT",EDGE,{"derivedFrom":[makeQuery(id+"F7.opExtrude","SWEPT_FACE",FACE,{"disambiguationData":[OSD([sQuery(id+"F6.wireOp",EDGE,"E31")])]}),makeQuery(id+"F16.opExtrude","SWEPT_FACE",FACE,{"disambiguationData":[OSD([sQuery(id+"F15.wireOp",EDGE,"E37.filletArc")])]})]})});
            var Q3;
            Q3=makeQuery(id+"F18.opBoolean","COPY",EDGE,{"derivedFrom":makeQuery(id+"F17.opBoolean","INTERSECT",EDGE,{"derivedFrom":[makeQuery(id+"F7.opExtrude","SWEPT_FACE",FACE,{"disambiguationData":[OSD([sQuery(id+"F6.wireOp",EDGE,"E31")])]}),makeQuery(id+"F16.opExtrude","SWEPT_FACE",FACE,{"disambiguationData":[OSD([sQuery(id+"F15.wireOp",EDGE,"E32")])]})]})});
            var Q4;
            Q4=makeQuery(id+"F18.opBoolean","COPY",EDGE,{"derivedFrom":makeQuery(id+"F17.opBoolean","INTERSECT",EDGE,{"derivedFrom":[makeQuery(id+"F7.opExtrude","SWEPT_FACE",FACE,{"disambiguationData":[OSD([sQuery(id+"F6.wireOp",EDGE,"E31")])]}),makeQuery(id+"F16.opExtrude","SWEPT_FACE",FACE,{"disambiguationData":[OSD([sQuery(id+"F15.wireOp",EDGE,"E38.filletArc")])]})]})});
            var Q5;
            Q5=makeQuery(id+"F18.opBoolean","COPY",EDGE,{"derivedFrom":makeQuery(id+"F17.opBoolean","INTERSECT",EDGE,{"derivedFrom":[makeQuery(id+"F7.opExtrude","SWEPT_FACE",FACE,{"disambiguationData":[OSD([sQuery(id+"F6.wireOp",EDGE,"E31")])]}),makeQuery(id+"F16.opExtrude","SWEPT_FACE",FACE,{"disambiguationData":[OSD([sQuery(id+"F15.wireOp",EDGE,"E33")])]})]})});
            var Q6;
            Q6=makeQuery(id+"F18.opBoolean","COPY",EDGE,{"derivedFrom":makeQuery(id+"F17.opBoolean","INTERSECT",EDGE,{"derivedFrom":[makeQuery(id+"F7.opExtrude","SWEPT_FACE",FACE,{"disambiguationData":[OSD([sQuery(id+"F6.wireOp",EDGE,"E31")])]}),makeQuery(id+"F16.opExtrude","SWEPT_FACE",FACE,{"disambiguationData":[OSD([sQuery(id+"F15.wireOp",EDGE,"E39.filletArc")])]})]})});
            var Q7;
            Q7=makeQuery(id+"F18.opBoolean","COPY",EDGE,{"derivedFrom":makeQuery(id+"F17.opBoolean","INTERSECT",EDGE,{"derivedFrom":[makeQuery(id+"F7.opExtrude","SWEPT_FACE",FACE,{"disambiguationData":[OSD([sQuery(id+"F6.wireOp",EDGE,"E31")])]}),makeQuery(id+"F16.opExtrude","SWEPT_FACE",FACE,{"disambiguationData":[OSD([sQuery(id+"F15.wireOp",EDGE,"E34")])]})]})});
            var Q8;
            Q8=makeQuery(id+"F18.opBoolean","COPY",EDGE,{"derivedFrom":makeQuery(id+"F17.opBoolean","INTERSECT",EDGE,{"derivedFrom":[makeQuery(id+"F7.opExtrude","SWEPT_FACE",FACE,{"disambiguationData":[OSD([sQuery(id+"F6.wireOp",EDGE,"E31")])]}),makeQuery(id+"F16.opExtrude","SWEPT_FACE",FACE,{"disambiguationData":[OSD([sQuery(id+"F15.wireOp",EDGE,"E40")])]})]})});
            var Q9;
            Q9=makeQuery(id+"F18.opBoolean","COPY",EDGE,{"derivedFrom":makeQuery(id+"F17.opBoolean","INTERSECT",EDGE,{"derivedFrom":[makeQuery(id+"F7.opExtrude","SWEPT_FACE",FACE,{"disambiguationData":[OSD([sQuery(id+"F6.wireOp",EDGE,"E31")])]}),makeQuery(id+"F16.opExtrude","SWEPT_FACE",FACE,{"disambiguationData":[OSD([sQuery(id+"F15.wireOp",EDGE,"E46.filletArc"),sQuery(id+"F15.wireOp",EDGE,"E47.filletArc")])]})]})});
            var Q10;
            Q10=makeQuery(id+"F18.opBoolean","COPY",EDGE,{"derivedFrom":makeQuery(id+"F17.opBoolean","INTERSECT",EDGE,{"derivedFrom":[makeQuery(id+"F7.opExtrude","SWEPT_FACE",FACE,{"disambiguationData":[OSD([sQuery(id+"F6.wireOp",EDGE,"E31")])]}),makeQuery(id+"F16.opExtrude","SWEPT_FACE",FACE,{"disambiguationData":[OSD([sQuery(id+"F15.wireOp",EDGE,"E44.filletArc"),sQuery(id+"F15.wireOp",EDGE,"E45.filletArc")])]})]})});
            var Q11;
            Q11=makeQuery(id+"F18.opBoolean","COPY",EDGE,{"derivedFrom":makeQuery(id+"F17.opBoolean","INTERSECT",EDGE,{"derivedFrom":[makeQuery(id+"F7.opExtrude","SWEPT_FACE",FACE,{"disambiguationData":[OSD([sQuery(id+"F6.wireOp",EDGE,"E31")])]}),makeQuery(id+"F16.opExtrude","SWEPT_FACE",FACE,{"disambiguationData":[OSD([sQuery(id+"F15.wireOp",EDGE,"E42")])]})]})});
            fillet(context, id + "F20", {"entities" : qUnion([Q0, Q1, Q2, Q3, Q4, Q5, Q6, Q7, Q8, Q9, Q10, Q11]), "radius" : 0.5 * mm, "tangentPropagation" : true, "allowEdgeOverflow" : false});
        }
        {
            var Q0;
            Q0=sQuery(id+"F2.wireOp",EDGE,"E13");
            cPlane(context, id + "F21", {"entities" : qUnion([Q0]), "cplaneType" : CPlaneType.LINE_ANGLE, "offset" : 152.4 * mm, "angle" : 240 * degree, "width" : 152.4 * mm, "height" : 152.4 * mm});
        }
        {
            var Q0;
            Q0=qCreatedBy(id+"F21.planeOp",FACE);
            cPlane(context, id + "F22", {"entities" : qUnion([Q0]), "cplaneType" : CPlaneType.OFFSET, "offset" : 15.88 * mm, "oppositeDirection" : true, "width" : 152.4 * mm, "height" : 152.4 * mm});
        }
        {
            var Q0;
            Q0=qCreatedBy(id+"F22.planeOp",FACE);
            var sketch = newSketch(context, id + "F23", { "sketchPlane" : qUnion([Q0])});
            skLineSegment(sketch, "E48", {"start": v(21.59, -2.8) * mm, "end": v(21.59, 2.8) * mm});
            skLineSegment(sketch, "E49", {"start": v(20.57, 3.8) * mm, "end": v(20.07, 3.8) * mm});
            skLineSegment(sketch, "E50", {"start": v(19.05, 2.8) * mm, "end": v(19.05, -0.25) * mm});
            skLineSegment(sketch, "E51", {"start": v(18.03, -1.27) * mm, "end": v(17.53, -1.27) * mm});
            skLineSegment(sketch, "E52", {"start": v(16.5, -0.25) * mm, "end": v(16.5, 2.16) * mm});
            skLineSegment(sketch, "E53", {"start": v(15.5, 3.17) * mm, "end": v(14.99, 3.17) * mm});
            skLineSegment(sketch, "E54", {"start": v(13.97, 2.16) * mm, "end": v(13.97, -0.25) * mm});
            skLineSegment(sketch, "E55", {"start": v(12.95, -1.27) * mm, "end": v(12.45, -1.27) * mm});
            skLineSegment(sketch, "E56", {"start": v(11.43, -0.25) * mm, "end": v(11.43, 2.8) * mm});
            skLineSegment(sketch, "E57", {"start": v(10.41, 3.81) * mm, "end": v(9.9, 3.81) * mm});
            skLineSegment(sketch, "E58", {"start": v(8.89, 2.8) * mm, "end": v(8.89, -2.8) * mm});
            skLineSegment(sketch, "E59", {"start": v(9.9, -3.8) * mm, "end": v(20.57, -3.81) * mm});
            skPoint(sketch, "E60.visualSharp", {"position": v(21.59, -3.81) * mm});
            skArc(sketch, "E60.filletArc", {"start": v(20.57, -3.81) * mm, "mid": v(21.3, -3.51) * mm, "end": v(21.59, -2.8) * mm});
            skPoint(sketch, "E61.visualSharp", {"position": v(21.59, 3.8) * mm});
            skArc(sketch, "E61.filletArc", {"start": v(21.59, 2.8) * mm, "mid": v(21.3, 3.51) * mm, "end": v(20.57, 3.81) * mm});
            skPoint(sketch, "E62.visualSharp", {"position": v(19.05, 3.8) * mm});
            skArc(sketch, "E62.filletArc", {"start": v(20.07, 3.8) * mm, "mid": v(19.35, 3.51) * mm, "end": v(19.05, 2.8) * mm});
            skPoint(sketch, "E63.visualSharp", {"position": v(19.05, -1.27) * mm});
            skArc(sketch, "E63.filletArc", {"start": v(18.03, -1.27) * mm, "mid": v(18.75, -0.97) * mm, "end": v(19.05, -0.25) * mm});
            skPoint(sketch, "E64.visualSharp", {"position": v(16.5, -1.27) * mm});
            skArc(sketch, "E64.filletArc", {"start": v(16.5, -0.25) * mm, "mid": v(16.8, -0.97) * mm, "end": v(17.53, -1.27) * mm});
            skPoint(sketch, "E65.visualSharp", {"position": v(16.5, 3.17) * mm});
            skArc(sketch, "E65.filletArc", {"start": v(16.5, 2.16) * mm, "mid": v(16.21, 2.88) * mm, "end": v(15.5, 3.17) * mm});
            skPoint(sketch, "E66.visualSharp", {"position": v(13.97, 3.17) * mm});
            skArc(sketch, "E66.filletArc", {"start": v(14.99, 3.17) * mm, "mid": v(14.27, 2.88) * mm, "end": v(13.97, 2.16) * mm});
            skPoint(sketch, "E67.visualSharp", {"position": v(13.97, -1.27) * mm});
            skArc(sketch, "E67.filletArc", {"start": v(12.95, -1.27) * mm, "mid": v(13.67, -0.97) * mm, "end": v(13.97, -0.25) * mm});
            skPoint(sketch, "E68.visualSharp", {"position": v(11.43, -1.27) * mm});
            skArc(sketch, "E68.filletArc", {"start": v(11.43, -0.25) * mm, "mid": v(11.73, -0.97) * mm, "end": v(12.45, -1.27) * mm});
            skPoint(sketch, "E69.visualSharp", {"position": v(11.43, 3.81) * mm});
            skArc(sketch, "E69.filletArc", {"start": v(11.43, 2.8) * mm, "mid": v(11.13, 3.51) * mm, "end": v(10.41, 3.81) * mm});
            skPoint(sketch, "E70.visualSharp", {"position": v(8.89, 3.81) * mm});
            skArc(sketch, "E70.filletArc", {"start": v(9.9, 3.81) * mm, "mid": v(9.19, 3.51) * mm, "end": v(8.89, 2.8) * mm});
            skPoint(sketch, "E71.visualSharp", {"position": v(8.89, -3.8) * mm});
            skArc(sketch, "E71.filletArc", {"start": v(8.89, -2.8) * mm, "mid": v(9.19, -3.51) * mm, "end": v(9.9, -3.81) * mm});
            skSolve(sketch);
        }
        {
            var Q0;
            Q0=qSketchRegion(id+"F23",true);
            extrude(context, id + "F24", {"entities" : qUnion([Q0]), "depth" : 25.4 * mm});
        }
        {
            var Q0;
            Q0=makeQuery(id+"F7.opExtrude","SWEPT_BODY",BODY,{"disambiguationData":[OSD([sQuery(id+"F6.wireOp",EDGE,"E31")])]});
            var Q1;
            Q1=makeQuery(id+"F24.opExtrude","SWEPT_BODY",BODY,{"disambiguationData":[OSD([sQuery(id+"F23.wireOp",EDGE,"E48"),sQuery(id+"F23.wireOp",EDGE,"E49"),sQuery(id+"F23.wireOp",EDGE,"E50"),sQuery(id+"F23.wireOp",EDGE,"E51"),sQuery(id+"F23.wireOp",EDGE,"E52"),sQuery(id+"F23.wireOp",EDGE,"E53"),sQuery(id+"F23.wireOp",EDGE,"E54"),sQuery(id+"F23.wireOp",EDGE,"E55"),sQuery(id+"F23.wireOp",EDGE,"E56"),sQuery(id+"F23.wireOp",EDGE,"E57"),sQuery(id+"F23.wireOp",EDGE,"E58"),sQuery(id+"F23.wireOp",EDGE,"E59"),sQuery(id+"F23.wireOp",EDGE,"E60.filletArc"),sQuery(id+"F23.wireOp",EDGE,"E61.filletArc"),sQuery(id+"F23.wireOp",EDGE,"E62.filletArc"),sQuery(id+"F23.wireOp",EDGE,"E63.filletArc"),sQuery(id+"F23.wireOp",EDGE,"E64.filletArc"),sQuery(id+"F23.wireOp",EDGE,"E65.filletArc"),sQuery(id+"F23.wireOp",EDGE,"E66.filletArc"),sQuery(id+"F23.wireOp",EDGE,"E67.filletArc"),sQuery(id+"F23.wireOp",EDGE,"E68.filletArc"),sQuery(id+"F23.wireOp",EDGE,"E69.filletArc"),sQuery(id+"F23.wireOp",EDGE,"E70.filletArc"),sQuery(id+"F23.wireOp",EDGE,"E71.filletArc")])]});
            booleanBodies(context, id + "F25", {"operationType" : BooleanOperationType.SUBTRACTION, "tools" : qUnion([Q0]), "targets" : qUnion([Q1]), "keepTools" : true});
        }
        {
            var Q0;
            Q0=makeQuery(id+"F24.opExtrude","SWEPT_BODY",BODY,{"disambiguationData":[OSD([sQuery(id+"F23.wireOp",EDGE,"E48"),sQuery(id+"F23.wireOp",EDGE,"E49"),sQuery(id+"F23.wireOp",EDGE,"E50"),sQuery(id+"F23.wireOp",EDGE,"E51"),sQuery(id+"F23.wireOp",EDGE,"E52"),sQuery(id+"F23.wireOp",EDGE,"E53"),sQuery(id+"F23.wireOp",EDGE,"E54"),sQuery(id+"F23.wireOp",EDGE,"E55"),sQuery(id+"F23.wireOp",EDGE,"E56"),sQuery(id+"F23.wireOp",EDGE,"E57"),sQuery(id+"F23.wireOp",EDGE,"E58"),sQuery(id+"F23.wireOp",EDGE,"E59"),sQuery(id+"F23.wireOp",EDGE,"E60.filletArc"),sQuery(id+"F23.wireOp",EDGE,"E61.filletArc"),sQuery(id+"F23.wireOp",EDGE,"E62.filletArc"),sQuery(id+"F23.wireOp",EDGE,"E63.filletArc"),sQuery(id+"F23.wireOp",EDGE,"E64.filletArc"),sQuery(id+"F23.wireOp",EDGE,"E65.filletArc"),sQuery(id+"F23.wireOp",EDGE,"E66.filletArc"),sQuery(id+"F23.wireOp",EDGE,"E67.filletArc"),sQuery(id+"F23.wireOp",EDGE,"E68.filletArc"),sQuery(id+"F23.wireOp",EDGE,"E69.filletArc"),sQuery(id+"F23.wireOp",EDGE,"E70.filletArc"),sQuery(id+"F23.wireOp",EDGE,"E71.filletArc")])]});
            var Q1;
            Q1=makeQuery(id+"F1.opExtrude","SWEPT_BODY",BODY,{"disambiguationData":[OSD([sQuery(id+"F0.wireOp",EDGE,"E0")])]});
            booleanBodies(context, id + "F26", {"operationType" : BooleanOperationType.SUBTRACTION, "tools" : qUnion([Q0]), "targets" : qUnion([Q1])});
        }
        {
            var Q0;
            {var subQ0=sQuery(id+"F0.wireOp",EDGE,"E0");Q0=makeQuery(id+"F26.opBoolean","INTERSECT",EDGE,{"derivedFrom":[makeQuery(id+"F18.opBoolean","SPLIT",FACE,{"disambiguationData":[TD([makeQuery(id+"F1.opExtrude","CAP_FACE",FACE,{"disambiguationData":[OSD([subQ0])],"isStart":true})])],"derivedFrom":makeQuery(id+"F1.opExtrude","SWEPT_FACE",FACE,{"disambiguationData":[OSD([subQ0])]})}),makeQuery(id+"F24.opExtrude","SWEPT_FACE",FACE,{"disambiguationData":[OSD([sQuery(id+"F23.wireOp",EDGE,"E59")])]})]});}
            var Q1;
            {var subQ0=sQuery(id+"F0.wireOp",EDGE,"E0");Q1=makeQuery(id+"F26.opBoolean","INTERSECT",EDGE,{"derivedFrom":[makeQuery(id+"F18.opBoolean","SPLIT",FACE,{"disambiguationData":[TD([makeQuery(id+"F1.opExtrude","CAP_FACE",FACE,{"disambiguationData":[OSD([subQ0])],"isStart":true})])],"derivedFrom":makeQuery(id+"F1.opExtrude","SWEPT_FACE",FACE,{"disambiguationData":[OSD([subQ0])]})}),makeQuery(id+"F24.opExtrude","SWEPT_FACE",FACE,{"disambiguationData":[OSD([sQuery(id+"F23.wireOp",EDGE,"E60.filletArc")])]})]});}
            var Q2;
            {var subQ0=sQuery(id+"F0.wireOp",EDGE,"E0");Q2=makeQuery(id+"F26.opBoolean","INTERSECT",EDGE,{"derivedFrom":[makeQuery(id+"F18.opBoolean","SPLIT",FACE,{"disambiguationData":[TD([makeQuery(id+"F1.opExtrude","CAP_FACE",FACE,{"disambiguationData":[OSD([subQ0])],"isStart":true})])],"derivedFrom":makeQuery(id+"F1.opExtrude","SWEPT_FACE",FACE,{"disambiguationData":[OSD([subQ0])]})}),makeQuery(id+"F24.opExtrude","SWEPT_FACE",FACE,{"disambiguationData":[OSD([sQuery(id+"F23.wireOp",EDGE,"E48")])]})]});}
            var Q3;
            {var subQ0=sQuery(id+"F0.wireOp",EDGE,"E0");Q3=makeQuery(id+"F26.opBoolean","INTERSECT",EDGE,{"derivedFrom":[makeQuery(id+"F18.opBoolean","SPLIT",FACE,{"disambiguationData":[TD([makeQuery(id+"F1.opExtrude","CAP_FACE",FACE,{"disambiguationData":[OSD([subQ0])],"isStart":true})])],"derivedFrom":makeQuery(id+"F1.opExtrude","SWEPT_FACE",FACE,{"disambiguationData":[OSD([subQ0])]})}),makeQuery(id+"F24.opExtrude","SWEPT_FACE",FACE,{"disambiguationData":[OSD([sQuery(id+"F23.wireOp",EDGE,"E61.filletArc")])]})]});}
            var Q4;
            {var subQ0=sQuery(id+"F0.wireOp",EDGE,"E0");Q4=makeQuery(id+"F26.opBoolean","INTERSECT",EDGE,{"derivedFrom":[makeQuery(id+"F18.opBoolean","SPLIT",FACE,{"disambiguationData":[TD([makeQuery(id+"F1.opExtrude","CAP_FACE",FACE,{"disambiguationData":[OSD([subQ0])],"isStart":true})])],"derivedFrom":makeQuery(id+"F1.opExtrude","SWEPT_FACE",FACE,{"disambiguationData":[OSD([subQ0])]})}),makeQuery(id+"F24.opExtrude","SWEPT_FACE",FACE,{"disambiguationData":[OSD([sQuery(id+"F23.wireOp",EDGE,"E49")])]})]});}
            var Q5;
            {var subQ0=sQuery(id+"F0.wireOp",EDGE,"E0");Q5=makeQuery(id+"F26.opBoolean","INTERSECT",EDGE,{"derivedFrom":[makeQuery(id+"F18.opBoolean","SPLIT",FACE,{"disambiguationData":[TD([makeQuery(id+"F1.opExtrude","CAP_FACE",FACE,{"disambiguationData":[OSD([subQ0])],"isStart":true})])],"derivedFrom":makeQuery(id+"F1.opExtrude","SWEPT_FACE",FACE,{"disambiguationData":[OSD([subQ0])]})}),makeQuery(id+"F24.opExtrude","SWEPT_FACE",FACE,{"disambiguationData":[OSD([sQuery(id+"F23.wireOp",EDGE,"E62.filletArc")])]})]});}
            var Q6;
            {var subQ0=sQuery(id+"F0.wireOp",EDGE,"E0");Q6=makeQuery(id+"F26.opBoolean","INTERSECT",EDGE,{"derivedFrom":[makeQuery(id+"F18.opBoolean","SPLIT",FACE,{"disambiguationData":[TD([makeQuery(id+"F1.opExtrude","CAP_FACE",FACE,{"disambiguationData":[OSD([subQ0])],"isStart":true})])],"derivedFrom":makeQuery(id+"F1.opExtrude","SWEPT_FACE",FACE,{"disambiguationData":[OSD([subQ0])]})}),makeQuery(id+"F24.opExtrude","SWEPT_FACE",FACE,{"disambiguationData":[OSD([sQuery(id+"F23.wireOp",EDGE,"E50")])]})]});}
            var Q7;
            {var subQ0=sQuery(id+"F0.wireOp",EDGE,"E0");Q7=makeQuery(id+"F26.opBoolean","INTERSECT",EDGE,{"derivedFrom":[makeQuery(id+"F18.opBoolean","SPLIT",FACE,{"disambiguationData":[TD([makeQuery(id+"F1.opExtrude","CAP_FACE",FACE,{"disambiguationData":[OSD([subQ0])],"isStart":true})])],"derivedFrom":makeQuery(id+"F1.opExtrude","SWEPT_FACE",FACE,{"disambiguationData":[OSD([subQ0])]})}),makeQuery(id+"F24.opExtrude","SWEPT_FACE",FACE,{"disambiguationData":[OSD([sQuery(id+"F23.wireOp",EDGE,"E63.filletArc")])]})]});}
            var Q8;
            {var subQ0=sQuery(id+"F0.wireOp",EDGE,"E0");Q8=makeQuery(id+"F26.opBoolean","INTERSECT",EDGE,{"derivedFrom":[makeQuery(id+"F18.opBoolean","SPLIT",FACE,{"disambiguationData":[TD([makeQuery(id+"F1.opExtrude","CAP_FACE",FACE,{"disambiguationData":[OSD([subQ0])],"isStart":true})])],"derivedFrom":makeQuery(id+"F1.opExtrude","SWEPT_FACE",FACE,{"disambiguationData":[OSD([subQ0])]})}),makeQuery(id+"F24.opExtrude","SWEPT_FACE",FACE,{"disambiguationData":[OSD([sQuery(id+"F23.wireOp",EDGE,"E64.filletArc")])]})]});}
            var Q9;
            {var subQ0=sQuery(id+"F0.wireOp",EDGE,"E0");Q9=makeQuery(id+"F26.opBoolean","INTERSECT",EDGE,{"derivedFrom":[makeQuery(id+"F18.opBoolean","SPLIT",FACE,{"disambiguationData":[TD([makeQuery(id+"F1.opExtrude","CAP_FACE",FACE,{"disambiguationData":[OSD([subQ0])],"isStart":true})])],"derivedFrom":makeQuery(id+"F1.opExtrude","SWEPT_FACE",FACE,{"disambiguationData":[OSD([subQ0])]})}),makeQuery(id+"F24.opExtrude","SWEPT_FACE",FACE,{"disambiguationData":[OSD([sQuery(id+"F23.wireOp",EDGE,"E51")])]})]});}
            var Q10;
            {var subQ0=sQuery(id+"F0.wireOp",EDGE,"E0");Q10=makeQuery(id+"F26.opBoolean","INTERSECT",EDGE,{"derivedFrom":[makeQuery(id+"F18.opBoolean","SPLIT",FACE,{"disambiguationData":[TD([makeQuery(id+"F1.opExtrude","CAP_FACE",FACE,{"disambiguationData":[OSD([subQ0])],"isStart":true})])],"derivedFrom":makeQuery(id+"F1.opExtrude","SWEPT_FACE",FACE,{"disambiguationData":[OSD([subQ0])]})}),makeQuery(id+"F24.opExtrude","SWEPT_FACE",FACE,{"disambiguationData":[OSD([sQuery(id+"F23.wireOp",EDGE,"E52")])]})]});}
            var Q11;
            {var subQ0=sQuery(id+"F0.wireOp",EDGE,"E0");Q11=makeQuery(id+"F26.opBoolean","INTERSECT",EDGE,{"derivedFrom":[makeQuery(id+"F18.opBoolean","SPLIT",FACE,{"disambiguationData":[TD([makeQuery(id+"F1.opExtrude","CAP_FACE",FACE,{"disambiguationData":[OSD([subQ0])],"isStart":true})])],"derivedFrom":makeQuery(id+"F1.opExtrude","SWEPT_FACE",FACE,{"disambiguationData":[OSD([subQ0])]})}),makeQuery(id+"F24.opExtrude","SWEPT_FACE",FACE,{"disambiguationData":[OSD([sQuery(id+"F23.wireOp",EDGE,"E65.filletArc")])]})]});}
            var Q12;
            {var subQ0=sQuery(id+"F0.wireOp",EDGE,"E0");Q12=makeQuery(id+"F26.opBoolean","INTERSECT",EDGE,{"derivedFrom":[makeQuery(id+"F18.opBoolean","SPLIT",FACE,{"disambiguationData":[TD([makeQuery(id+"F1.opExtrude","CAP_FACE",FACE,{"disambiguationData":[OSD([subQ0])],"isStart":true})])],"derivedFrom":makeQuery(id+"F1.opExtrude","SWEPT_FACE",FACE,{"disambiguationData":[OSD([subQ0])]})}),makeQuery(id+"F24.opExtrude","SWEPT_FACE",FACE,{"disambiguationData":[OSD([sQuery(id+"F23.wireOp",EDGE,"E53")])]})]});}
            var Q13;
            {var subQ0=sQuery(id+"F0.wireOp",EDGE,"E0");Q13=makeQuery(id+"F26.opBoolean","INTERSECT",EDGE,{"derivedFrom":[makeQuery(id+"F18.opBoolean","SPLIT",FACE,{"disambiguationData":[TD([makeQuery(id+"F1.opExtrude","CAP_FACE",FACE,{"disambiguationData":[OSD([subQ0])],"isStart":true})])],"derivedFrom":makeQuery(id+"F1.opExtrude","SWEPT_FACE",FACE,{"disambiguationData":[OSD([subQ0])]})}),makeQuery(id+"F24.opExtrude","SWEPT_FACE",FACE,{"disambiguationData":[OSD([sQuery(id+"F23.wireOp",EDGE,"E66.filletArc")])]})]});}
            var Q14;
            {var subQ0=sQuery(id+"F0.wireOp",EDGE,"E0");Q14=makeQuery(id+"F26.opBoolean","INTERSECT",EDGE,{"derivedFrom":[makeQuery(id+"F18.opBoolean","SPLIT",FACE,{"disambiguationData":[TD([makeQuery(id+"F1.opExtrude","CAP_FACE",FACE,{"disambiguationData":[OSD([subQ0])],"isStart":true})])],"derivedFrom":makeQuery(id+"F1.opExtrude","SWEPT_FACE",FACE,{"disambiguationData":[OSD([subQ0])]})}),makeQuery(id+"F24.opExtrude","SWEPT_FACE",FACE,{"disambiguationData":[OSD([sQuery(id+"F23.wireOp",EDGE,"E54")])]})]});}
            var Q15;
            {var subQ0=sQuery(id+"F0.wireOp",EDGE,"E0");Q15=makeQuery(id+"F26.opBoolean","INTERSECT",EDGE,{"derivedFrom":[makeQuery(id+"F18.opBoolean","SPLIT",FACE,{"disambiguationData":[TD([makeQuery(id+"F1.opExtrude","CAP_FACE",FACE,{"disambiguationData":[OSD([subQ0])],"isStart":true})])],"derivedFrom":makeQuery(id+"F1.opExtrude","SWEPT_FACE",FACE,{"disambiguationData":[OSD([subQ0])]})}),makeQuery(id+"F24.opExtrude","SWEPT_FACE",FACE,{"disambiguationData":[OSD([sQuery(id+"F23.wireOp",EDGE,"E67.filletArc")])]})]});}
            var Q16;
            {var subQ0=sQuery(id+"F0.wireOp",EDGE,"E0");Q16=makeQuery(id+"F26.opBoolean","INTERSECT",EDGE,{"derivedFrom":[makeQuery(id+"F18.opBoolean","SPLIT",FACE,{"disambiguationData":[TD([makeQuery(id+"F1.opExtrude","CAP_FACE",FACE,{"disambiguationData":[OSD([subQ0])],"isStart":true})])],"derivedFrom":makeQuery(id+"F1.opExtrude","SWEPT_FACE",FACE,{"disambiguationData":[OSD([subQ0])]})}),makeQuery(id+"F24.opExtrude","SWEPT_FACE",FACE,{"disambiguationData":[OSD([sQuery(id+"F23.wireOp",EDGE,"E55")])]})]});}
            var Q17;
            {var subQ0=sQuery(id+"F0.wireOp",EDGE,"E0");Q17=makeQuery(id+"F26.opBoolean","INTERSECT",EDGE,{"derivedFrom":[makeQuery(id+"F18.opBoolean","SPLIT",FACE,{"disambiguationData":[TD([makeQuery(id+"F1.opExtrude","CAP_FACE",FACE,{"disambiguationData":[OSD([subQ0])],"isStart":true})])],"derivedFrom":makeQuery(id+"F1.opExtrude","SWEPT_FACE",FACE,{"disambiguationData":[OSD([subQ0])]})}),makeQuery(id+"F24.opExtrude","SWEPT_FACE",FACE,{"disambiguationData":[OSD([sQuery(id+"F23.wireOp",EDGE,"E68.filletArc")])]})]});}
            var Q18;
            {var subQ0=sQuery(id+"F0.wireOp",EDGE,"E0");Q18=makeQuery(id+"F26.opBoolean","INTERSECT",EDGE,{"derivedFrom":[makeQuery(id+"F18.opBoolean","SPLIT",FACE,{"disambiguationData":[TD([makeQuery(id+"F1.opExtrude","CAP_FACE",FACE,{"disambiguationData":[OSD([subQ0])],"isStart":true})])],"derivedFrom":makeQuery(id+"F1.opExtrude","SWEPT_FACE",FACE,{"disambiguationData":[OSD([subQ0])]})}),makeQuery(id+"F24.opExtrude","SWEPT_FACE",FACE,{"disambiguationData":[OSD([sQuery(id+"F23.wireOp",EDGE,"E56")])]})]});}
            var Q19;
            {var subQ0=sQuery(id+"F0.wireOp",EDGE,"E0");Q19=makeQuery(id+"F26.opBoolean","INTERSECT",EDGE,{"derivedFrom":[makeQuery(id+"F18.opBoolean","SPLIT",FACE,{"disambiguationData":[TD([makeQuery(id+"F1.opExtrude","CAP_FACE",FACE,{"disambiguationData":[OSD([subQ0])],"isStart":true})])],"derivedFrom":makeQuery(id+"F1.opExtrude","SWEPT_FACE",FACE,{"disambiguationData":[OSD([subQ0])]})}),makeQuery(id+"F24.opExtrude","SWEPT_FACE",FACE,{"disambiguationData":[OSD([sQuery(id+"F23.wireOp",EDGE,"E69.filletArc")])]})]});}
            var Q20;
            {var subQ0=sQuery(id+"F0.wireOp",EDGE,"E0");Q20=makeQuery(id+"F26.opBoolean","INTERSECT",EDGE,{"derivedFrom":[makeQuery(id+"F18.opBoolean","SPLIT",FACE,{"disambiguationData":[TD([makeQuery(id+"F1.opExtrude","CAP_FACE",FACE,{"disambiguationData":[OSD([subQ0])],"isStart":true})])],"derivedFrom":makeQuery(id+"F1.opExtrude","SWEPT_FACE",FACE,{"disambiguationData":[OSD([subQ0])]})}),makeQuery(id+"F24.opExtrude","SWEPT_FACE",FACE,{"disambiguationData":[OSD([sQuery(id+"F23.wireOp",EDGE,"E57")])]})]});}
            var Q21;
            {var subQ0=sQuery(id+"F0.wireOp",EDGE,"E0");Q21=makeQuery(id+"F26.opBoolean","INTERSECT",EDGE,{"derivedFrom":[makeQuery(id+"F18.opBoolean","SPLIT",FACE,{"disambiguationData":[TD([makeQuery(id+"F1.opExtrude","CAP_FACE",FACE,{"disambiguationData":[OSD([subQ0])],"isStart":true})])],"derivedFrom":makeQuery(id+"F1.opExtrude","SWEPT_FACE",FACE,{"disambiguationData":[OSD([subQ0])]})}),makeQuery(id+"F24.opExtrude","SWEPT_FACE",FACE,{"disambiguationData":[OSD([sQuery(id+"F23.wireOp",EDGE,"E70.filletArc")])]})]});}
            var Q22;
            {var subQ0=sQuery(id+"F0.wireOp",EDGE,"E0");Q22=makeQuery(id+"F26.opBoolean","INTERSECT",EDGE,{"derivedFrom":[makeQuery(id+"F18.opBoolean","SPLIT",FACE,{"disambiguationData":[TD([makeQuery(id+"F1.opExtrude","CAP_FACE",FACE,{"disambiguationData":[OSD([subQ0])],"isStart":true})])],"derivedFrom":makeQuery(id+"F1.opExtrude","SWEPT_FACE",FACE,{"disambiguationData":[OSD([subQ0])]})}),makeQuery(id+"F24.opExtrude","SWEPT_FACE",FACE,{"disambiguationData":[OSD([sQuery(id+"F23.wireOp",EDGE,"E58")])]})]});}
            var Q23;
            {var subQ0=sQuery(id+"F0.wireOp",EDGE,"E0");Q23=makeQuery(id+"F26.opBoolean","INTERSECT",EDGE,{"derivedFrom":[makeQuery(id+"F18.opBoolean","SPLIT",FACE,{"disambiguationData":[TD([makeQuery(id+"F1.opExtrude","CAP_FACE",FACE,{"disambiguationData":[OSD([subQ0])],"isStart":true})])],"derivedFrom":makeQuery(id+"F1.opExtrude","SWEPT_FACE",FACE,{"disambiguationData":[OSD([subQ0])]})}),makeQuery(id+"F24.opExtrude","SWEPT_FACE",FACE,{"disambiguationData":[OSD([sQuery(id+"F23.wireOp",EDGE,"E71.filletArc")])]})]});}
            var Q24;
            Q24=makeQuery(id+"F26.opBoolean","COPY",EDGE,{"derivedFrom":makeQuery(id+"F25.opBoolean","INTERSECT",EDGE,{"derivedFrom":[makeQuery(id+"F7.opExtrude","SWEPT_FACE",FACE,{"disambiguationData":[OSD([sQuery(id+"F6.wireOp",EDGE,"E31")])]}),makeQuery(id+"F24.opExtrude","SWEPT_FACE",FACE,{"disambiguationData":[OSD([sQuery(id+"F23.wireOp",EDGE,"E59")])]})]})});
            var Q25;
            Q25=makeQuery(id+"F26.opBoolean","COPY",EDGE,{"derivedFrom":makeQuery(id+"F25.opBoolean","INTERSECT",EDGE,{"derivedFrom":[makeQuery(id+"F7.opExtrude","SWEPT_FACE",FACE,{"disambiguationData":[OSD([sQuery(id+"F6.wireOp",EDGE,"E31")])]}),makeQuery(id+"F24.opExtrude","SWEPT_FACE",FACE,{"disambiguationData":[OSD([sQuery(id+"F23.wireOp",EDGE,"E60.filletArc")])]})]})});
            var Q26;
            Q26=makeQuery(id+"F26.opBoolean","COPY",EDGE,{"derivedFrom":makeQuery(id+"F25.opBoolean","INTERSECT",EDGE,{"derivedFrom":[makeQuery(id+"F7.opExtrude","SWEPT_FACE",FACE,{"disambiguationData":[OSD([sQuery(id+"F6.wireOp",EDGE,"E31")])]}),makeQuery(id+"F24.opExtrude","SWEPT_FACE",FACE,{"disambiguationData":[OSD([sQuery(id+"F23.wireOp",EDGE,"E48")])]})]})});
            var Q27;
            Q27=makeQuery(id+"F26.opBoolean","COPY",EDGE,{"derivedFrom":makeQuery(id+"F25.opBoolean","INTERSECT",EDGE,{"derivedFrom":[makeQuery(id+"F7.opExtrude","SWEPT_FACE",FACE,{"disambiguationData":[OSD([sQuery(id+"F6.wireOp",EDGE,"E31")])]}),makeQuery(id+"F24.opExtrude","SWEPT_FACE",FACE,{"disambiguationData":[OSD([sQuery(id+"F23.wireOp",EDGE,"E61.filletArc")])]})]})});
            var Q28;
            Q28=makeQuery(id+"F26.opBoolean","COPY",EDGE,{"derivedFrom":makeQuery(id+"F25.opBoolean","INTERSECT",EDGE,{"derivedFrom":[makeQuery(id+"F7.opExtrude","SWEPT_FACE",FACE,{"disambiguationData":[OSD([sQuery(id+"F6.wireOp",EDGE,"E31")])]}),makeQuery(id+"F24.opExtrude","SWEPT_FACE",FACE,{"disambiguationData":[OSD([sQuery(id+"F23.wireOp",EDGE,"E49")])]})]})});
            var Q29;
            Q29=makeQuery(id+"F26.opBoolean","COPY",EDGE,{"derivedFrom":makeQuery(id+"F25.opBoolean","INTERSECT",EDGE,{"derivedFrom":[makeQuery(id+"F7.opExtrude","SWEPT_FACE",FACE,{"disambiguationData":[OSD([sQuery(id+"F6.wireOp",EDGE,"E31")])]}),makeQuery(id+"F24.opExtrude","SWEPT_FACE",FACE,{"disambiguationData":[OSD([sQuery(id+"F23.wireOp",EDGE,"E62.filletArc")])]})]})});
            var Q30;
            Q30=makeQuery(id+"F26.opBoolean","COPY",EDGE,{"derivedFrom":makeQuery(id+"F25.opBoolean","INTERSECT",EDGE,{"derivedFrom":[makeQuery(id+"F7.opExtrude","SWEPT_FACE",FACE,{"disambiguationData":[OSD([sQuery(id+"F6.wireOp",EDGE,"E31")])]}),makeQuery(id+"F24.opExtrude","SWEPT_FACE",FACE,{"disambiguationData":[OSD([sQuery(id+"F23.wireOp",EDGE,"E63.filletArc")])]})]})});
            var Q31;
            Q31=makeQuery(id+"F26.opBoolean","COPY",EDGE,{"derivedFrom":makeQuery(id+"F25.opBoolean","INTERSECT",EDGE,{"derivedFrom":[makeQuery(id+"F7.opExtrude","SWEPT_FACE",FACE,{"disambiguationData":[OSD([sQuery(id+"F6.wireOp",EDGE,"E31")])]}),makeQuery(id+"F24.opExtrude","SWEPT_FACE",FACE,{"disambiguationData":[OSD([sQuery(id+"F23.wireOp",EDGE,"E51")])]})]})});
            var Q32;
            Q32=makeQuery(id+"F26.opBoolean","COPY",EDGE,{"derivedFrom":makeQuery(id+"F25.opBoolean","INTERSECT",EDGE,{"derivedFrom":[makeQuery(id+"F7.opExtrude","SWEPT_FACE",FACE,{"disambiguationData":[OSD([sQuery(id+"F6.wireOp",EDGE,"E31")])]}),makeQuery(id+"F24.opExtrude","SWEPT_FACE",FACE,{"disambiguationData":[OSD([sQuery(id+"F23.wireOp",EDGE,"E64.filletArc")])]})]})});
            var Q33;
            Q33=makeQuery(id+"F26.opBoolean","COPY",EDGE,{"derivedFrom":makeQuery(id+"F25.opBoolean","INTERSECT",EDGE,{"derivedFrom":[makeQuery(id+"F7.opExtrude","SWEPT_FACE",FACE,{"disambiguationData":[OSD([sQuery(id+"F6.wireOp",EDGE,"E31")])]}),makeQuery(id+"F24.opExtrude","SWEPT_FACE",FACE,{"disambiguationData":[OSD([sQuery(id+"F23.wireOp",EDGE,"E65.filletArc")])]})]})});
            var Q34;
            Q34=makeQuery(id+"F26.opBoolean","COPY",EDGE,{"derivedFrom":makeQuery(id+"F25.opBoolean","INTERSECT",EDGE,{"derivedFrom":[makeQuery(id+"F7.opExtrude","SWEPT_FACE",FACE,{"disambiguationData":[OSD([sQuery(id+"F6.wireOp",EDGE,"E31")])]}),makeQuery(id+"F24.opExtrude","SWEPT_FACE",FACE,{"disambiguationData":[OSD([sQuery(id+"F23.wireOp",EDGE,"E53")])]})]})});
            var Q35;
            Q35=makeQuery(id+"F26.opBoolean","COPY",EDGE,{"derivedFrom":makeQuery(id+"F25.opBoolean","INTERSECT",EDGE,{"derivedFrom":[makeQuery(id+"F7.opExtrude","SWEPT_FACE",FACE,{"disambiguationData":[OSD([sQuery(id+"F6.wireOp",EDGE,"E31")])]}),makeQuery(id+"F24.opExtrude","SWEPT_FACE",FACE,{"disambiguationData":[OSD([sQuery(id+"F23.wireOp",EDGE,"E66.filletArc")])]})]})});
            var Q36;
            Q36=makeQuery(id+"F26.opBoolean","COPY",EDGE,{"derivedFrom":makeQuery(id+"F25.opBoolean","INTERSECT",EDGE,{"derivedFrom":[makeQuery(id+"F7.opExtrude","SWEPT_FACE",FACE,{"disambiguationData":[OSD([sQuery(id+"F6.wireOp",EDGE,"E31")])]}),makeQuery(id+"F24.opExtrude","SWEPT_FACE",FACE,{"disambiguationData":[OSD([sQuery(id+"F23.wireOp",EDGE,"E67.filletArc")])]})]})});
            var Q37;
            Q37=makeQuery(id+"F26.opBoolean","COPY",EDGE,{"derivedFrom":makeQuery(id+"F25.opBoolean","INTERSECT",EDGE,{"derivedFrom":[makeQuery(id+"F7.opExtrude","SWEPT_FACE",FACE,{"disambiguationData":[OSD([sQuery(id+"F6.wireOp",EDGE,"E31")])]}),makeQuery(id+"F24.opExtrude","SWEPT_FACE",FACE,{"disambiguationData":[OSD([sQuery(id+"F23.wireOp",EDGE,"E55")])]})]})});
            var Q38;
            Q38=makeQuery(id+"F26.opBoolean","COPY",EDGE,{"derivedFrom":makeQuery(id+"F25.opBoolean","INTERSECT",EDGE,{"derivedFrom":[makeQuery(id+"F7.opExtrude","SWEPT_FACE",FACE,{"disambiguationData":[OSD([sQuery(id+"F6.wireOp",EDGE,"E31")])]}),makeQuery(id+"F24.opExtrude","SWEPT_FACE",FACE,{"disambiguationData":[OSD([sQuery(id+"F23.wireOp",EDGE,"E68.filletArc")])]})]})});
            var Q39;
            Q39=makeQuery(id+"F26.opBoolean","COPY",EDGE,{"derivedFrom":makeQuery(id+"F25.opBoolean","INTERSECT",EDGE,{"derivedFrom":[makeQuery(id+"F7.opExtrude","SWEPT_FACE",FACE,{"disambiguationData":[OSD([sQuery(id+"F6.wireOp",EDGE,"E31")])]}),makeQuery(id+"F24.opExtrude","SWEPT_FACE",FACE,{"disambiguationData":[OSD([sQuery(id+"F23.wireOp",EDGE,"E69.filletArc")])]})]})});
            var Q40;
            Q40=makeQuery(id+"F26.opBoolean","COPY",EDGE,{"derivedFrom":makeQuery(id+"F25.opBoolean","INTERSECT",EDGE,{"derivedFrom":[makeQuery(id+"F7.opExtrude","SWEPT_FACE",FACE,{"disambiguationData":[OSD([sQuery(id+"F6.wireOp",EDGE,"E31")])]}),makeQuery(id+"F24.opExtrude","SWEPT_FACE",FACE,{"disambiguationData":[OSD([sQuery(id+"F23.wireOp",EDGE,"E57")])]})]})});
            var Q41;
            Q41=makeQuery(id+"F26.opBoolean","COPY",EDGE,{"derivedFrom":makeQuery(id+"F25.opBoolean","INTERSECT",EDGE,{"derivedFrom":[makeQuery(id+"F7.opExtrude","SWEPT_FACE",FACE,{"disambiguationData":[OSD([sQuery(id+"F6.wireOp",EDGE,"E31")])]}),makeQuery(id+"F24.opExtrude","SWEPT_FACE",FACE,{"disambiguationData":[OSD([sQuery(id+"F23.wireOp",EDGE,"E70.filletArc")])]})]})});
            var Q42;
            Q42=makeQuery(id+"F26.opBoolean","COPY",EDGE,{"derivedFrom":makeQuery(id+"F25.opBoolean","INTERSECT",EDGE,{"derivedFrom":[makeQuery(id+"F7.opExtrude","SWEPT_FACE",FACE,{"disambiguationData":[OSD([sQuery(id+"F6.wireOp",EDGE,"E31")])]}),makeQuery(id+"F24.opExtrude","SWEPT_FACE",FACE,{"disambiguationData":[OSD([sQuery(id+"F23.wireOp",EDGE,"E58")])]})]})});
            var Q43;
            Q43=makeQuery(id+"F26.opBoolean","COPY",EDGE,{"derivedFrom":makeQuery(id+"F25.opBoolean","INTERSECT",EDGE,{"derivedFrom":[makeQuery(id+"F7.opExtrude","SWEPT_FACE",FACE,{"disambiguationData":[OSD([sQuery(id+"F6.wireOp",EDGE,"E31")])]}),makeQuery(id+"F24.opExtrude","SWEPT_FACE",FACE,{"disambiguationData":[OSD([sQuery(id+"F23.wireOp",EDGE,"E71.filletArc")])]})]})});
            var Q44;
            Q44=makeQuery(id+"F26.opBoolean","COPY",EDGE,{"derivedFrom":makeQuery(id+"F25.opBoolean","INTERSECT",EDGE,{"derivedFrom":[makeQuery(id+"F7.opExtrude","SWEPT_FACE",FACE,{"disambiguationData":[OSD([sQuery(id+"F6.wireOp",EDGE,"E31")])]}),makeQuery(id+"F24.opExtrude","SWEPT_FACE",FACE,{"disambiguationData":[OSD([sQuery(id+"F23.wireOp",EDGE,"E52")])]})]})});
            var Q45;
            Q45=makeQuery(id+"F26.opBoolean","COPY",EDGE,{"derivedFrom":makeQuery(id+"F25.opBoolean","INTERSECT",EDGE,{"derivedFrom":[makeQuery(id+"F7.opExtrude","SWEPT_FACE",FACE,{"disambiguationData":[OSD([sQuery(id+"F6.wireOp",EDGE,"E31")])]}),makeQuery(id+"F24.opExtrude","SWEPT_FACE",FACE,{"disambiguationData":[OSD([sQuery(id+"F23.wireOp",EDGE,"E56")])]})]})});
            var Q46;
            Q46=makeQuery(id+"F26.opBoolean","COPY",EDGE,{"derivedFrom":makeQuery(id+"F25.opBoolean","INTERSECT",EDGE,{"derivedFrom":[makeQuery(id+"F7.opExtrude","SWEPT_FACE",FACE,{"disambiguationData":[OSD([sQuery(id+"F6.wireOp",EDGE,"E31")])]}),makeQuery(id+"F24.opExtrude","SWEPT_FACE",FACE,{"disambiguationData":[OSD([sQuery(id+"F23.wireOp",EDGE,"E54")])]})]})});
            var Q47;
            Q47=makeQuery(id+"F26.opBoolean","COPY",EDGE,{"derivedFrom":makeQuery(id+"F25.opBoolean","INTERSECT",EDGE,{"derivedFrom":[makeQuery(id+"F7.opExtrude","SWEPT_FACE",FACE,{"disambiguationData":[OSD([sQuery(id+"F6.wireOp",EDGE,"E31")])]}),makeQuery(id+"F24.opExtrude","SWEPT_FACE",FACE,{"disambiguationData":[OSD([sQuery(id+"F23.wireOp",EDGE,"E50")])]})]})});
            fillet(context, id + "F27", {"entities" : qUnion([Q0, Q1, Q2, Q3, Q4, Q5, Q6, Q7, Q8, Q9, Q10, Q11, Q12, Q13, Q14, Q15, Q16, Q17, Q18, Q19, Q20, Q21, Q22, Q23, Q24, Q25, Q26, Q27, Q28, Q29, Q30, Q31, Q32, Q33, Q34, Q35, Q36, Q37, Q38, Q39, Q40, Q41, Q42, Q43, Q44, Q45, Q46, Q47]), "radius" : 0.5 * mm, "tangentPropagation" : true, "allowEdgeOverflow" : false});
        }
        {
            var Q0;
            Q0=makeQuery(id+"F1.opExtrude","CAP_FACE",FACE,{"disambiguationData":[OSD([sQuery(id+"F0.wireOp",EDGE,"E0")])],"isStart":false});
            extrude(context, id + "F28", {"entities" : qUnion([Q0]), "operationType" : NewBodyOperationType.ADD, "depth" : 3.8 * mm});
        }
        {
            var Q0;
            Q0=makeQuery(id+"F28.opExtrude","CAP_FACE",FACE,{"disambiguationData":[OSD([sQuery(id+"F0.wireOp",EDGE,"E0")])],"isStart":false});
            var sketch = newSketch(context, id + "F29", { "sketchPlane" : qUnion([Q0])});
            skLineSegment(sketch, "E72", {"start": v(12.29, 3.5) * mm, "end": v(-7.36, -30.53) * mm});
            skCircle(sketch, "E73", {"center": v(9.9, -5.71) * mm, "radius": 2.54 * mm});
            skLineSegment(sketch, "E74", {"start": v(0, 0) * mm, "end": v(7.7, -4.44) * mm});
            skSolve(sketch);
        }
        {
            var Q0;
            Q0=makeQuery(id+"F29.imprint","IMPRINT",FACE,{"disambiguationData":[TD([[makeQuery(id+"F29.imprint","IMPRINT",EDGE,{"derivedFrom":sQuery(id+"F29.wireOp",EDGE,"E73")}),1.0]])]});
            extrude(context, id + "F30", {"entities" : qUnion([Q0]), "operationType" : NewBodyOperationType.ADD, "depth" : 25.4 * mm});
        }
    });
